FCSTD DOCUMENT  (FreeCAD 0.21RUnknown)
Label: part4
License: All rights reserved
LicenseURL: https://en.wikipedia.org/wiki/All_rights_reserved
objects: Image::ImagePlane×1, Sketcher::SketchObject×1
note: 1 computed .brp shape members not serialized (recipe doc carries the construction recipe); baked Part::Feature solids carry a one-line shape summary decoded from their .brp

FEATURE [Image::ImagePlane] gasketflange1
  Placement = pos=(0,10,0) rot=(0,0,1;0rad)
  XSize = 118.028
  YSize = 113.509
FEATURE [Sketcher::SketchObject] Sketch
  FullyConstrained = true
  sketch-geometry (19):
    g0: Circle CenterX=0 CenterY=0 CenterZ=0 NormalX=0 NormalY=0 NormalZ=1 AngleXU=0 Radius=35
    g1: Circle CenterX=-47.1984 CenterY=-27.25 CenterZ=0 NormalX=0 NormalY=0 NormalZ=1 AngleXU=0 Radius=5
    g2: LineSegment StartX=0 StartY=0 StartZ=0 EndX=-47.1984 EndY=-27.25 EndZ=0
    g3: Circle CenterX=47.1984 CenterY=-27.25 CenterZ=0 NormalX=0 NormalY=0 NormalZ=1 AngleXU=0 Radius=5
    g4: LineSegment StartX=0 StartY=0 StartZ=0 EndX=47.1984 EndY=-27.25 EndZ=0
    g5: Circle CenterX=1.4e-15 CenterY=54.5 CenterZ=0 NormalX=0 NormalY=0 NormalZ=1 AngleXU=0 Radius=5
    g6: LineSegment StartX=0 StartY=0 StartZ=0 EndX=1.4e-15 EndY=54.5 EndZ=0
    g7: ArcOfCircle CenterX=1.4e-15 CenterY=54.5 CenterZ=0 NormalX=0 NormalY=0 NormalZ=1 AngleXU=0 Radius=11 StartAngle=0.698626 EndAngle=2.44297
    g8: LineSegment StartX=8.42299 StartY=61.5748 StartZ=0 EndX=34.4712 EndY=30.5629 EndZ=0
    g9: ArcOfCircle CenterX=47.1984 CenterY=-27.25 CenterZ=0 NormalX=0 NormalY=0 NormalZ=1 AngleXU=0 Radius=11 StartAngle=4.88742 EndAngle=6.63176
    g10: LineSegment StartX=57.5369 StartY=-23.4929 StartZ=0 EndX=43.7039 EndY=14.5715 EndZ=0
    g11: ArcOfCircle CenterX=-6.1276 CenterY=-3.53777 CenterZ=0 NormalX=0 NormalY=0 NormalZ=1 AngleXU=0 Radius=53.02 StartAngle=0.348572 EndAngle=0.698626
    g12: ArcOfCircle CenterX=6.1276 CenterY=-3.53777 CenterZ=0 NormalX=0 NormalY=0 NormalZ=1 AngleXU=0 Radius=53.02 StartAngle=2.44297 EndAngle=2.79302
    g13: LineSegment StartX=-34.4712 StartY=30.5629 StartZ=0 EndX=-8.42299 EndY=61.5748 EndZ=0
    g14: LineSegment StartX=-43.7039 StartY=14.5715 StartZ=0 EndX=-57.5369 EndY=-23.4929 EndZ=0
    g15: LineSegment StartX=49.1139 StartY=-38.0819 StartZ=0 EndX=9.23264 EndY=-45.1344 EndZ=0
    g16: LineSegment StartX=-9.23264 StartY=-45.1344 StartZ=0 EndX=-49.1139 EndY=-38.0819 EndZ=0
    g17: ArcOfCircle CenterX=-1.41e-14 CenterY=7.07554 CenterZ=0 NormalX=0 NormalY=0 NormalZ=1 AngleXU=0 Radius=53.02 StartAngle=4.53736 EndAngle=4.88742
    g18: ArcOfCircle CenterX=-47.1984 CenterY=-27.25 CenterZ=0 NormalX=0 NormalY=0 NormalZ=1 AngleXU=0 Radius=11 StartAngle=2.79302 EndAngle=4.53736
  constraints (44):
    c: Coincident(g0,g-1)
    c: Diameter(g0) = 70
    c: Diameter(g1) = 10
    c: Coincident(g2,g0)
    c: Coincident(g2,g1)
    c: Coincident(g4,g0)
    c: Coincident(g4,g3)
    c: Angle(g2,g4) = 2.0944
    c: Equal(g2,g4)
    c: Equal(g1,g3)
    c: Coincident(g6,g0)
    c: Coincident(g6,g5)
    c: Angle(g4,g6) = 2.0944
    c: Equal(g6,g4)
    c: DistanceY(g6,g6) = 54.5
    c: Equal(g5,g3)
    c: Coincident(g7,g5)
    c: Symmetric(g7,g7,g-2)
    c: Radius(g7) = 11
    c: Tangent(g8,g7) = 1.5708
    c: Coincident(g9,g3)
    c: Tangent(g10,g9) = -1.5708
    c: Equal(g10,g8)
    c: Tangent(g11,g10) = -1.5708
    c: Tangent(g11,g8) = 1.5708
    c: Radius(g11) = 53.02
    c: Coincident(g13,g7)
    c: Coincident(g18,g1)
    c: Tangent(g18,g14) = -1.5708
    c: Tangent(g18,g16) = 1.5708
    c: Tangent(g17,g16) = 1.5708
    c: Tangent(g17,g15) = 1.5708
    c: Tangent(g14,g12) = -1.5708
    c: Tangent(g13,g12) = 1.5708
    c: Equal(g14,g13)
    c: Equal(g13,g8)
    c: Equal(g10,g15)
    c: Equal(g15,g16)
    c: Equal(g11,g12)
    c: Equal(g12,g17)
    c: Distance(g8) = 40.5
    c: Tangent(g15,g9) = 1.5708
    c: Equal(g9,g18)
    c: Equal(g18,g7)
